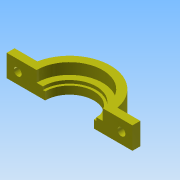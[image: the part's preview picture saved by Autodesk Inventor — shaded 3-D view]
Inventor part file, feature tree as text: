
AUTODESK INVENTOR PART (.ipt)
format: ipt  version: 2015 (Build 190159000, 159)  size: 119,808 bytes
history: native  units: mm
features: extrude x5, sketch x5
ambient origin geometry x8: Origin, YZ Plane, XZ Plane, XY Plane, X Axis, Y Axis, Z Axis, Center Point
bodies: 实体1 (feature_tree)
feature tree (10):
  extrude  "拉伸1"  Depth=5.0mm
  extrude  "拉伸2"  Depth=14.0mm TaperAngle=0.0deg
  extrude  "拉伸3"  Depth=7.0mm TaperAngle=0.0deg
  extrude  "拉伸4"  Depth=2.0mm TaperAngle=0.0deg
  extrude  "拉伸5"  Depth=5.0mm TaperAngle=0.0deg
  sketch  "草图1"  dims[d0=80.0mm d1=5.0mm]
  sketch  "草图2"  dims[d2=26.0mm d3=14.0mm d4=0.0mm]
  sketch  "草图3"  dims[d5=42.0mm d6=7.0mm d7=0.0mm]
  sketch  "草图4"  dims[d8=34.0mm d9=2.0mm d10=0.0mm]
  sketch  "草图5"  dims[d11=31.0mm d12=5.0mm d13=0.0mm d14=5.0mm d15=5.0mm d16=7.0mm d17=7.0mm d18=7.0mm d19=7.0mm d20=5.0mm d21=0.0mm]
